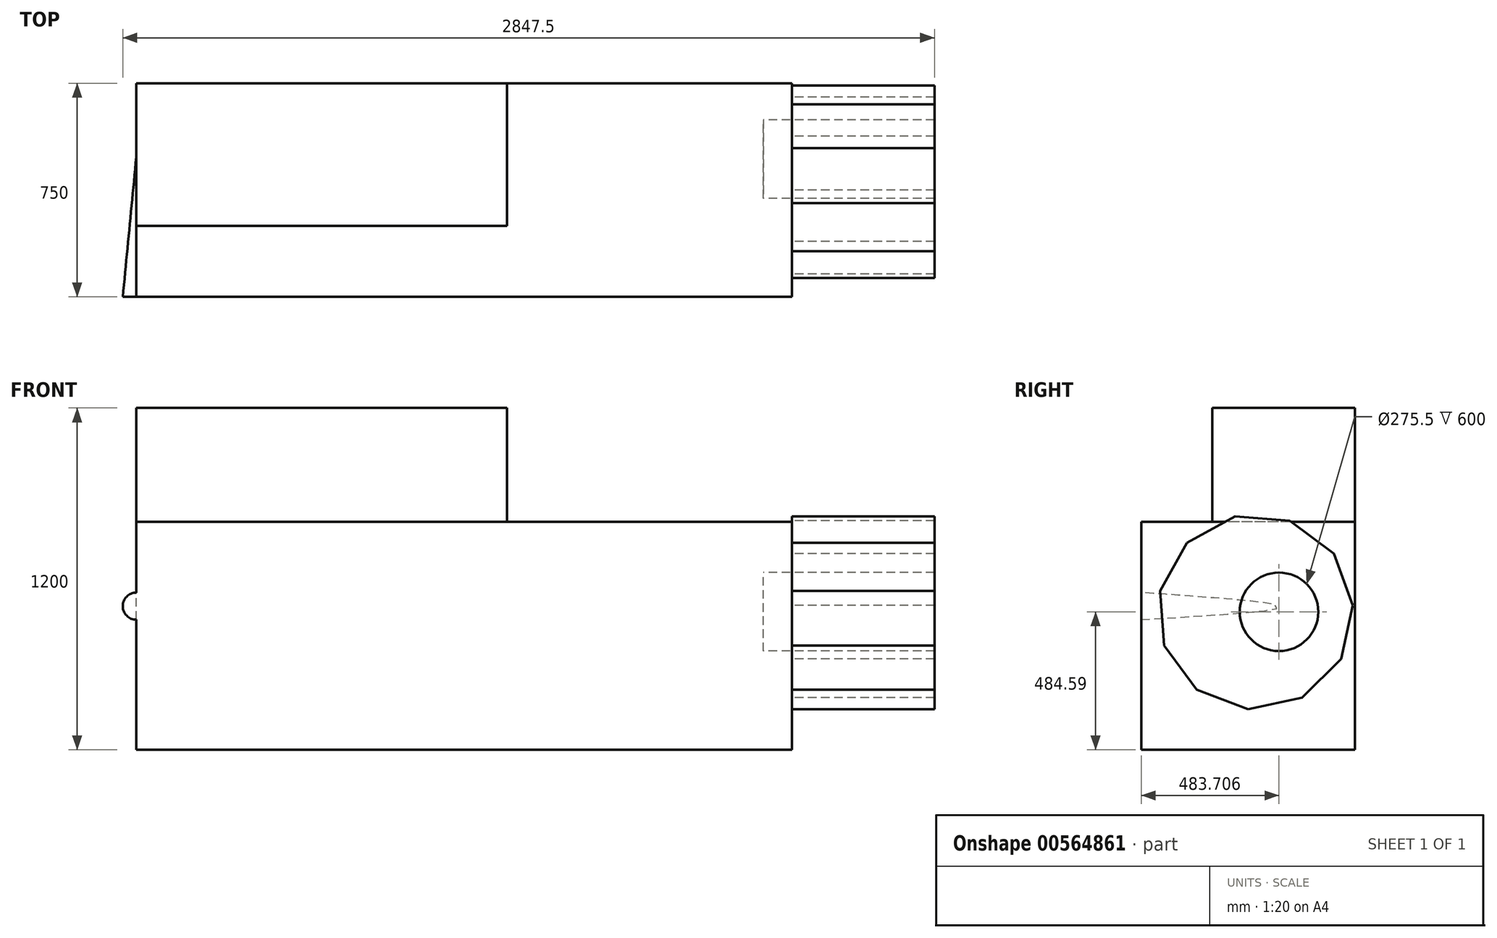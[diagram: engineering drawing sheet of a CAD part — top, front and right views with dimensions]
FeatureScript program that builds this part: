
annotation { "Feature Type Name" : "Feature", "Feature Type Description" : "" }
export const myFeature = defineFeature(function(context is Context, id is Id, definition is map)
    precondition{}
    {
        {
            var Q0;
            Q0=qCreatedBy(makeId("Right.planeOp"),FACE);
            var sketch = newSketch(context, id + "F0", { "sketchPlane" : qUnion([Q0])});
            skLineSegment(sketch, "E0.bottom", {"start": v(0, 315.41) * mm, "end": v(-500, 315.41) * mm});
            skLineSegment(sketch, "E0.top", {"start": v(0, 715.41) * mm, "end": v(-500, 715.41) * mm});
            skLineSegment(sketch, "E0.left", {"start": v(0, 315.41) * mm, "end": v(0, 715.41) * mm});
            skLineSegment(sketch, "E0.right", {"start": v(-500, 315.41) * mm, "end": v(-500, 715.41) * mm});
            skSolve(sketch);
        }
        {
            var Q0;
            Q0=makeQuery(id+"F0.imprint","IMPRINT",FACE,{"disambiguationData":[TD([[makeQuery(id+"F0.imprint","IMPRINT",EDGE,{"derivedFrom":sQuery(id+"F0.wireOp",EDGE,"E0.bottom")}),-1.0]])]});
            extrude(context, id + "F1", {"entities" : qUnion([Q0]), "depth" : 1300 * mm, "offsetDistance" : 25 * mm});
        }
        {
            var Q0;
            Q0=makeQuery(id+"F0.imprint","IMPRINT",FACE,{"disambiguationData":[TD([[makeQuery(id+"F0.imprint","IMPRINT",EDGE,{"derivedFrom":sQuery(id+"F0.wireOp",EDGE,"E0.bottom")}),-1.0]])]});
            var sketch = newSketch(context, id + "F2", { "sketchPlane" : qUnion([Q0])});
            skLineSegment(sketch, "E1.0", {"start": v(0, 315.41) * mm, "end": v(-750, 315.41) * mm});
            skLineSegment(sketch, "E2", {"start": v(-750, 315.41) * mm, "end": v(-750, -484.59) * mm});
            skLineSegment(sketch, "E3", {"start": v(-750, -484.59) * mm, "end": v(0, -484.59) * mm});
            skLineSegment(sketch, "E4", {"start": v(0, -484.59) * mm, "end": v(0, 315.41) * mm});
            skSolve(sketch);
        }
        {
            var Q0;
            {var subQ0=sQuery(id+"F2.wireOp",EDGE,"E2");Q0=makeQuery(id+"F2.imprint","IMPRINT",FACE,{"disambiguationData":[TD([[makeQuery(id+"F2.imprint","IMPRINT",EDGE,{"derivedFrom":subQ0}),1.0]])]});}
            extrude(context, id + "F3", {"entities" : qUnion([Q0]), "operationType" : NewBodyOperationType.ADD, "depth" : 2300 * mm, "offsetDistance" : 25 * mm});
        }
        {
            var Q0;
            Q0=makeQuery(id+"F3.opExtrude","CAP_FACE",FACE,{"disambiguationData":[OSD([sQuery(id+"F2.wireOp",EDGE,"E1.0"),sQuery(id+"F2.wireOp",EDGE,"E2"),sQuery(id+"F2.wireOp",EDGE,"E3"),sQuery(id+"F2.wireOp",EDGE,"E4")])],"isStart":false});
            var sketch = newSketch(context, id + "F4", { "sketchPlane" : qUnion([Q0])});
            skCircle(sketch, "E5.cCircle", {"center": v(-348.76, 0) * mm, "radius": 328.46 * mm, "construction": true});
            skLineSegment(sketch, "E5.0", {"start": v(-228.02, 320.32) * mm, "end": v(-74, 204.2) * mm});
            skLineSegment(sketch, "E5.1", {"start": v(-74, 204.2) * mm, "end": v(-7.22, 23.24) * mm});
            skLineSegment(sketch, "E5.2", {"start": v(-7.22, 23.24) * mm, "end": v(-48.88, -165.1) * mm});
            skLineSegment(sketch, "E5.3", {"start": v(-48.88, -165.1) * mm, "end": v(-185.74, -301.02) * mm});
            skLineSegment(sketch, "E5.4", {"start": v(-185.74, -301.02) * mm, "end": v(-374.36, -341.37) * mm});
            skLineSegment(sketch, "E5.5", {"start": v(-374.36, -341.37) * mm, "end": v(-554.85, -273.33) * mm});
            skLineSegment(sketch, "E5.6", {"start": v(-554.85, -273.33) * mm, "end": v(-669.91, -118.52) * mm});
            skLineSegment(sketch, "E5.7", {"start": v(-669.91, -118.52) * mm, "end": v(-683, 73.93) * mm});
            skLineSegment(sketch, "E5.8", {"start": v(-683, 73.93) * mm, "end": v(-589.98, 242.9) * mm});
            skLineSegment(sketch, "E5.9", {"start": v(-589.98, 242.9) * mm, "end": v(-420.36, 334.75) * mm});
            skLineSegment(sketch, "E5.10", {"start": v(-420.36, 334.75) * mm, "end": v(-228.02, 320.32) * mm});
            skPoint(sketch, "E5.0.midPoint", {"position": v(-151, 262.26) * mm});
            skSolve(sketch);
        }
        {
            var Q0;
            Q0 = qSketchRegion(id + "F4", true);
            extrude(context, id + "F5", {"entities" : qUnion([Q0]), "operationType" : NewBodyOperationType.ADD, "depth" : 500 * mm, "offsetDistance" : 25 * mm});
        }
        {
            var Q0;
            Q0=makeQuery(id+"F5.opExtrude","CAP_FACE",FACE,{"disambiguationData":[OSD([sQuery(id+"F4.wireOp",EDGE,"E5.0"),sQuery(id+"F4.wireOp",EDGE,"E5.1"),sQuery(id+"F4.wireOp",EDGE,"E5.2"),sQuery(id+"F4.wireOp",EDGE,"E5.3"),sQuery(id+"F4.wireOp",EDGE,"E5.4"),sQuery(id+"F4.wireOp",EDGE,"E5.5"),sQuery(id+"F4.wireOp",EDGE,"E5.6"),sQuery(id+"F4.wireOp",EDGE,"E5.7"),sQuery(id+"F4.wireOp",EDGE,"E5.8"),sQuery(id+"F4.wireOp",EDGE,"E5.9"),sQuery(id+"F4.wireOp",EDGE,"E5.10")])],"isStart":false});
            var sketch = newSketch(context, id + "F6", { "sketchPlane" : qUnion([Q0])});
            skSolve(sketch);
        }
        {
            var Q0;
            Q0=makeQuery(id+"F6.imprint","IMPRINT",FACE,{"disambiguationData":[TD([[makeQuery(id+"F6.imprint","IMPRINT",EDGE,{"derivedFrom":makeQuery(id+"F5.opExtrude","CAP_EDGE",EDGE,{"disambiguationData":[OSD([sQuery(id+"F4.wireOp",EDGE,"E5.0")])],"isStart":false})}),-1.0]])]});
            var sketch = newSketch(context, id + "F7", { "sketchPlane" : qUnion([Q0])});
            skCircle(sketch, "E6", {"center": v(-266.3, 0) * mm, "radius": 137.75 * mm});
            skSolve(sketch);
        }
        {
            var Q0;
            Q0 = qSketchRegion(id + "F7", true);
            extrude(context, id + "F8", {"entities" : qUnion([Q0]), "operationType" : NewBodyOperationType.REMOVE, "oppositeDirection" : true, "depth" : 600 * mm, "offsetDistance" : 25 * mm, "hasDraft" : true, "draftAngle" : 0 * degree});
        }
        {
            var Q0;
            Q0=qCreatedBy(makeId("Front.planeOp"),FACE);
            var sketch = newSketch(context, id + "F9", { "sketchPlane" : qUnion([Q0])});
            skCircle(sketch, "E7", {"center": v(24.96, 16.65) * mm, "radius": 30 * mm, "construction": true});
            skSolve(sketch);
        }
        {
            var Q0;
            Q0=makeQuery(id+"F3.opExtrude","SWEPT_FACE",FACE,{"disambiguationData":[OSD([sQuery(id+"F2.wireOp",EDGE,"E2")])]});
            var sketch = newSketch(context, id + "F10", { "sketchPlane" : qUnion([Q0])});
            skCircle(sketch, "E8", {"center": v(0, 20) * mm, "radius": 47.5 * mm});
            skSolve(sketch);
        }
        {
            var Q1;
            Q1=sQuery(id+"F9.wireOp",VERTEX,"E7.center");
            var Q2;
            Q2=makeQuery(id+"F10.imprint","IMPRINT",FACE,{"disambiguationData":[TD([[makeQuery(id+"F10.imprint","IMPRINT",EDGE,{"derivedFrom":sQuery(id+"F10.wireOp",EDGE,"E8")}),1.0]])]});
            loft(context, id + "F11", {"operationType" : NewBodyOperationType.ADD, "sheetProfilesArray" : [{ "sheetProfileEntities" : qUnion([Q1]) }, { "sheetProfileEntities" : qUnion([Q2]) }]});
        }
    });
